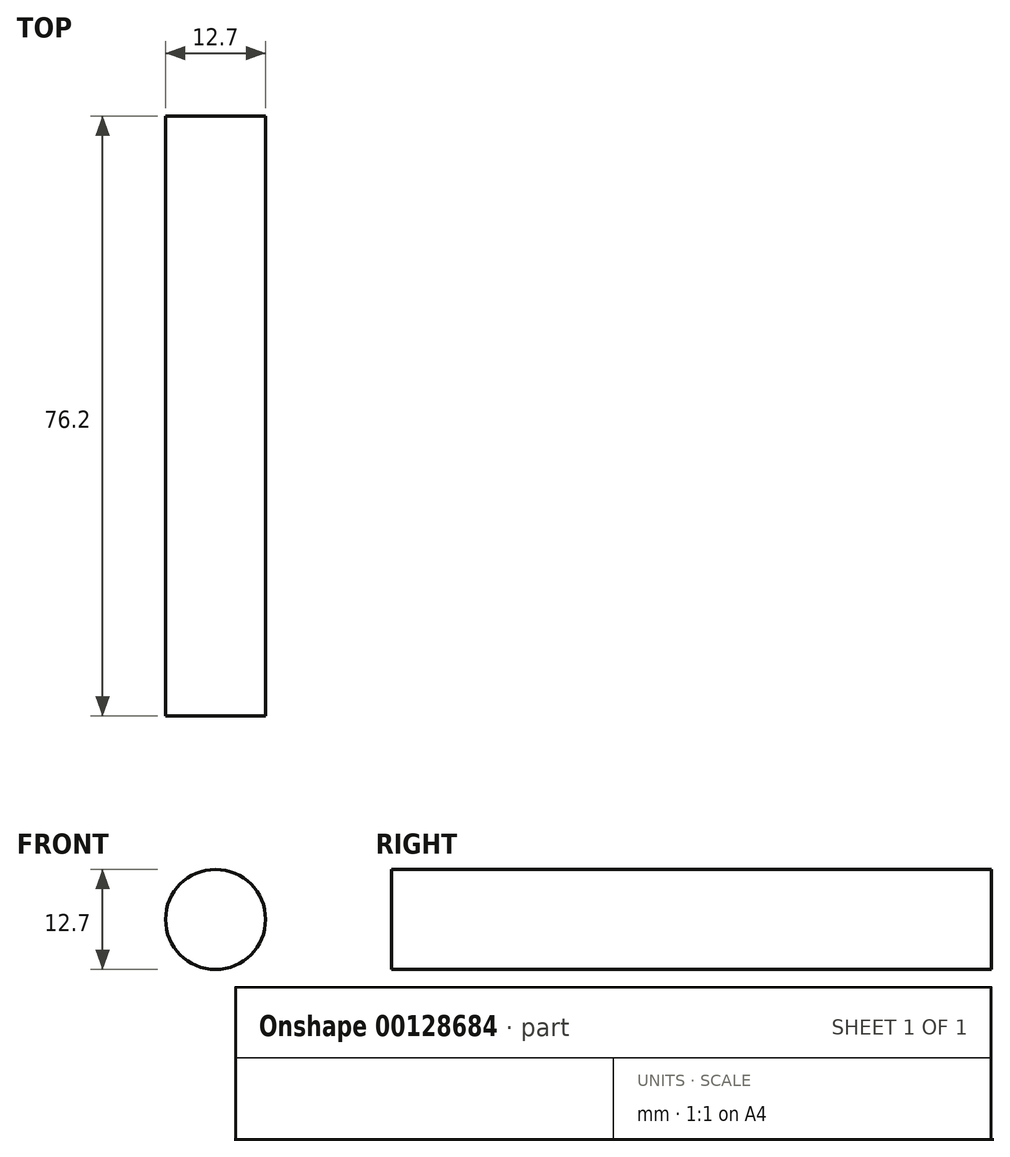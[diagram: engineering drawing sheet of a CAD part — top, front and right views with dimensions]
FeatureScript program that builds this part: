
annotation { "Feature Type Name" : "Feature", "Feature Type Description" : "" }
export const myFeature = defineFeature(function(context is Context, id is Id, definition is map)
    precondition{}
    {
        {
            var Q0;
            Q0=qCreatedBy(makeId("Front.planeOp"),FACE);
            var sketch = newSketch(context, id + "F0", { "sketchPlane" : qUnion([Q0])});
            skCircle(sketch, "E0", {"center": v(0, 114.3) * mm, "radius": 6.35 * mm});
            skSolve(sketch);
        }
        {
            var Q0;
            Q0 = qSketchRegion(id + "F0", true);
            extrude(context, id + "F1", {"entities" : qUnion([Q0]), "depth" : 76.2 * mm});
        }
    });
